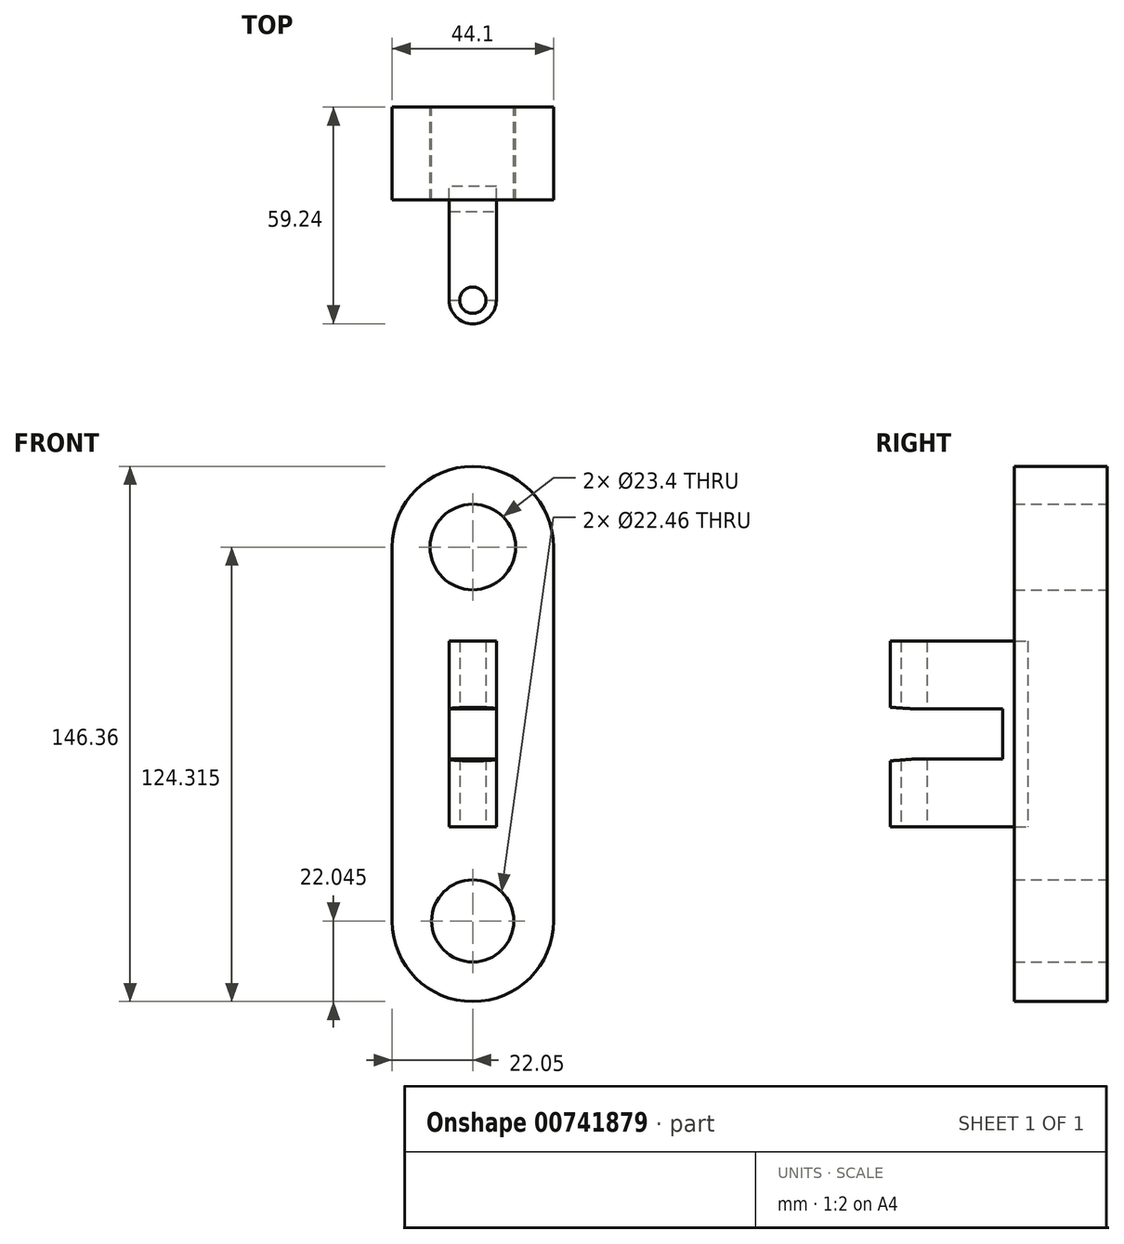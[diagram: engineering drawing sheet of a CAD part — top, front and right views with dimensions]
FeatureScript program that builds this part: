
annotation { "Feature Type Name" : "Feature", "Feature Type Description" : "" }
export const myFeature = defineFeature(function(context is Context, id is Id, definition is map)
    precondition{}
    {
        {
            var Q0;
            Q0=qCreatedBy(makeId("Front.planeOp"),FACE);
            var sketch = newSketch(context, id + "F0", { "sketchPlane" : qUnion([Q0])});
            skLineSegment(sketch, "E0.left", {"start": v(22.05, 51.14) * mm, "end": v(22.05, -51.14) * mm});
            skLineSegment(sketch, "E0.right", {"start": v(-22.05, 51.14) * mm, "end": v(-22.05, -51.14) * mm});
            skPoint(sketch, "E0.middle", {"position": v(0, 0) * mm});
            skArc(sketch, "E1", {"start": v(22.05, 51.14) * mm, "mid": v(0, 73.18) * mm, "end": v(-22.05, 51.14) * mm});
            skArc(sketch, "E2", {"start": v(-22.05, -51.14) * mm, "mid": v(0, -73.18) * mm, "end": v(22.05, -51.14) * mm});
            skCircle(sketch, "E3", {"center": v(0, 51.14) * mm, "radius": 11.7 * mm});
            skCircle(sketch, "E4", {"center": v(0, -51.14) * mm, "radius": 11.23 * mm});
            skSolve(sketch);
        }
        {
            var Q0;
            Q0=makeQuery(id+"F0.imprint","IMPRINT",FACE,{"disambiguationData":[TD([[makeQuery(id+"F0.imprint","IMPRINT",EDGE,{"derivedFrom":sQuery(id+"F0.wireOp",EDGE,"E0.left")}),-1.0]])]});
            var sketch = newSketch(context, id + "F1", { "sketchPlane" : qUnion([Q0])});
            skLineSegment(sketch, "E5.bottom", {"start": v(13.53, 31.19) * mm, "end": v(-13.53, 31.19) * mm});
            skLineSegment(sketch, "E5.top", {"start": v(13.53, -31.19) * mm, "end": v(-13.53, -31.19) * mm});
            skLineSegment(sketch, "E5.left", {"start": v(13.53, 31.19) * mm, "end": v(13.53, -31.19) * mm});
            skLineSegment(sketch, "E5.right", {"start": v(-13.53, 31.19) * mm, "end": v(-13.53, -31.19) * mm});
            skPoint(sketch, "E5.middle", {"position": v(0, 0) * mm});
            skSolve(sketch);
        }
        {
            var Q0;
            Q0=makeQuery(id+"F0.imprint","IMPRINT",FACE,{"disambiguationData":[TD([[makeQuery(id+"F0.imprint","IMPRINT",EDGE,{"derivedFrom":sQuery(id+"F0.wireOp",EDGE,"E0.left")}),-1.0]])]});
            var Q1;
            Q1=makeQuery(id+"F1.imprint","IMPRINT",FACE,{"disambiguationData":[TD([[makeQuery(id+"F1.imprint","IMPRINT",EDGE,{"derivedFrom":sQuery(id+"F1.wireOp",EDGE,"E5.bottom")}),-1.0]])]});
            var Q2;
            Q2=makeQuery(id+"F1.imprint","IMPRINT",FACE,{"disambiguationData":[TD([[makeQuery(id+"F1.imprint","IMPRINT",EDGE,{"derivedFrom":sQuery(id+"F1.wireOp",EDGE,"E5.bottom")}),1.0]])]});
            extrude(context, id + "F2", {"entities" : qUnion([Q0, Q1, Q2]), "depth" : 25.4 * mm, "offsetDistance" : 25.4 * mm});
        }
        {
            var Q0;
            Q0=qCreatedBy(makeId("Top.planeOp"),FACE);
            var sketch = newSketch(context, id + "F3", { "sketchPlane" : qUnion([Q0])});
            skLineSegment(sketch, "E6.bottom", {"start": v(6.45, -52.8) * mm, "end": v(-6.45, -52.8) * mm});
            skLineSegment(sketch, "E6.top", {"start": v(6.45, -21.69) * mm, "end": v(-6.45, -21.69) * mm});
            skLineSegment(sketch, "E6.left", {"start": v(6.45, -52.8) * mm, "end": v(6.45, -21.69) * mm});
            skLineSegment(sketch, "E6.right", {"start": v(-6.45, -52.8) * mm, "end": v(-6.45, -21.69) * mm});
            skPoint(sketch, "E6.middle", {"position": v(0, -37.24) * mm});
            skCircle(sketch, "E7", {"center": v(0, -52.8) * mm, "radius": 6.45 * mm});
            skCircle(sketch, "E8", {"center": v(0, -52.8) * mm, "radius": 3.6 * mm});
            skSolve(sketch);
        }
        {
            var Q0;
            Q0=makeQuery(id+"F3.imprint","IMPRINT",FACE,{"disambiguationData":[TD([[makeQuery(id+"F3.imprint","IMPRINT",EDGE,{"derivedFrom":sQuery(id+"F3.wireOp",EDGE,"E6.top")}),1.0]])]});
            var Q1;
            {var subQ1=sQuery(id+"F3.wireOp",EDGE,"E6.bottom");var subQ3=sQuery(id+"F3.wireOp",EDGE,"E8");var subQ4=makeQuery(id+"F3.imprint","INTERSECT",VERTEX,{"disambiguationData":[OD(0.0)],"derivedFrom":[subQ1,subQ3]});Q1=makeQuery(id+"F3.imprint","IMPRINT",FACE,{"disambiguationData":[TD([[makeQuery(id+"F3.imprint","IMPRINT",EDGE,{"disambiguationData":[TD([[subQ4,-1.0]])],"derivedFrom":subQ3}),-1.0]])]});}
            var Q2;
            {var subQ1=sQuery(id+"F3.wireOp",EDGE,"E6.bottom");var subQ3=sQuery(id+"F3.wireOp",EDGE,"E8");var subQ4=makeQuery(id+"F3.imprint","INTERSECT",VERTEX,{"disambiguationData":[OD(0.0)],"derivedFrom":[subQ1,subQ3]});Q2=makeQuery(id+"F3.imprint","IMPRINT",FACE,{"disambiguationData":[TD([[makeQuery(id+"F3.imprint","IMPRINT",EDGE,{"disambiguationData":[TD([[subQ4,1.0]])],"derivedFrom":subQ3}),-1.0]])]});}
            extrude(context, id + "F4", {"entities" : qUnion([Q0, Q1, Q2]), "depth" : 25.4 * mm, "offsetDistance" : 25.4 * mm, "hasSecondDirection" : true, "secondDirectionOppositeDirection" : true, "secondDirectionDepth" : 25.4 * mm});
        }
        {
            var Q0;
            Q0=makeQuery(id+"F4.opExtrude","SWEPT_FACE",FACE,{"disambiguationData":[OSD([sQuery(id+"F3.wireOp",EDGE,"E6.left")])]});
            var sketch = newSketch(context, id + "F5", { "sketchPlane" : qUnion([Q0])});
            skLineSegment(sketch, "E9.bottom", {"start": v(-52.8, 6.86) * mm, "end": v(-28.51, 6.86) * mm});
            skLineSegment(sketch, "E9.top", {"start": v(-52.8, -6.86) * mm, "end": v(-28.51, -6.86) * mm});
            skLineSegment(sketch, "E9.left", {"start": v(-52.8, 6.86) * mm, "end": v(-52.8, -6.86) * mm});
            skLineSegment(sketch, "E9.right", {"start": v(-28.51, 6.86) * mm, "end": v(-28.51, -6.86) * mm});
            skPoint(sketch, "E9.middle", {"position": v(-40.65, 0) * mm});
            skCircle(sketch, "E10", {"center": v(-52.8, 0) * mm, "radius": 6.86 * mm});
            skLineSegment(sketch, "E11", {"start": v(-59.66, 0) * mm, "end": v(-59.66, 7.34) * mm});
            skLineSegment(sketch, "E12", {"start": v(-59.66, 7.34) * mm, "end": v(-52.8, 6.86) * mm});
            skLineSegment(sketch, "E13", {"start": v(-59.66, 0) * mm, "end": v(-59.66, -7.37) * mm});
            skLineSegment(sketch, "E14", {"start": v(-59.66, -7.37) * mm, "end": v(-52.8, -6.86) * mm});
            skSolve(sketch);
        }
        {
            var Q0;
            Q0 = qSketchRegion(id + "F5", true);
            extrude(context, id + "F6", {"entities" : qUnion([Q0]), "operationType" : NewBodyOperationType.REMOVE, "oppositeDirection" : true, "depth" : 25.4 * mm, "offsetDistance" : 25.4 * mm});
        }
    });
